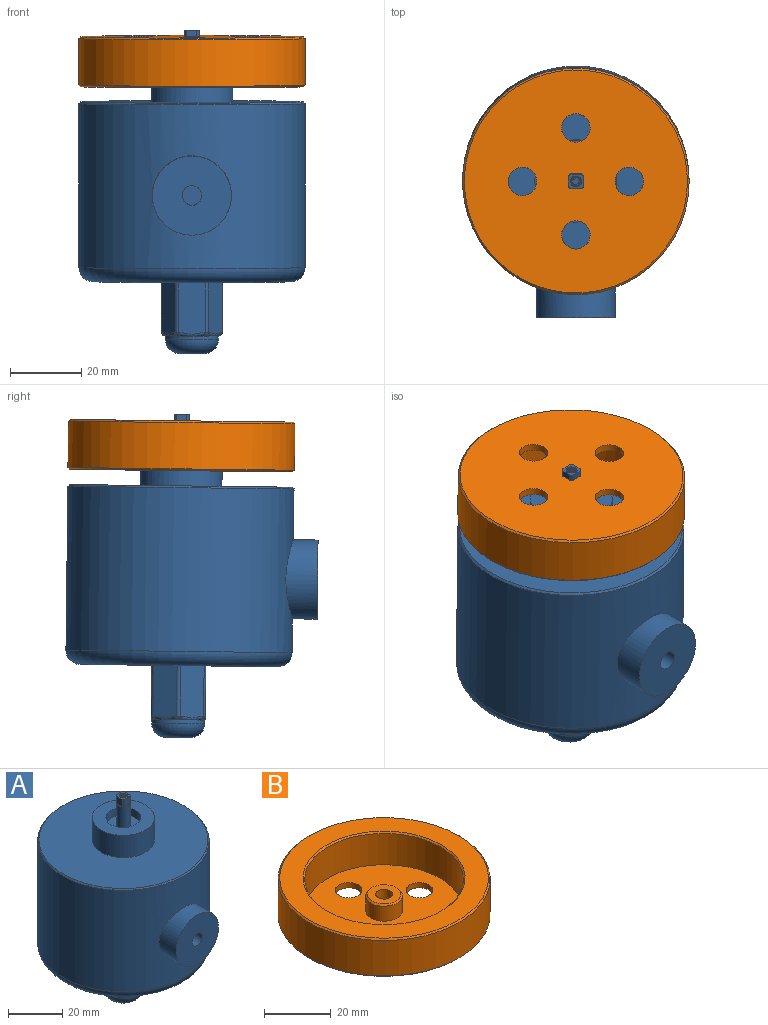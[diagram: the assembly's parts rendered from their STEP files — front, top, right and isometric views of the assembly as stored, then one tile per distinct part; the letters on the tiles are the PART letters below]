
ASSEMBLY  parts=2 mates=1
PART A: 73 faces, bbox 68.9x73.2x91.1 mm
  f0: plane 2.88x2.87mm, normal (0,0,1), area 5.9mm2, adj f69,f70,f71,f72
  f1: plane 4.31x4.31mm, normal (0,0,1), area 10.6mm2, adj f2,f60,f62,f64,f66,f69,f70,f71
  f2: cylinder r=2.5mm len=13.5mm, axis (0,0,-1), area 173.5mm2, adj f1,f58,f59,f60,f61,f62,f63,f64
  f3: plane 0.53x0.31mm, normal (0,0,-1), area 0.1mm2, adj f24,f29,f30
  f4: plane 0.53x0.31mm, normal (0,0,-1), area 0.1mm2, adj f24,f35,f40
  f5: plane 0.61x0.18mm, normal (0,0,-1), area 0.1mm2, adj f24,f45,f50
  f6: plane 0.53x0.31mm, normal (0,0,-1), area 0.1mm2, adj f24,f53,f54
  f7: plane 0.61x0.18mm, normal (0,0,-1), area 0.1mm2, adj f24,f34,f39
  f8: plane 55.5x55.5mm, normal (0,0,-1), area 2219.5mm2, adj f13,f17,f18,f19,f20,f21,f22,f27
  f9: cylinder r=31.75mm len=63.5mm, axis (0,0,-1), area 8773.2mm2, adj f11,f13,f14
  f10: plane 62.5x62.5mm, normal (0,0,1), area 2652.5mm2, adj f14,f15
  f11: cylinder r=11.11mm len=22.21mm, axis (0,1,0), area 551mm2, adj f9,f12
  f12: plane 22.21x22.21mm, normal (0,-1,0), area 363.7mm2, adj f11,f67
  f13: torus R=27.75mm, axis (0,0,1), area 1196.1mm2, adj f8,f9
  f14: cone r=31.25mm half-angle=45deg, axis (0,0,-1), area 140mm2, adj f9,f10
  f15: cylinder r=11.5mm len=23mm, axis (0,0,-1), area 727.6mm2, adj f10,f16
  f16: plane 23x23mm, normal (0,0,1), area 284.8mm2, adj f15,f57
  f17: plane 14.67x7.62mm, normal (0,-1,0), area 109.8mm2, adj f8,f43,f49,f51,f53,f56
  f18: plane 14.67x6.6mm, normal (-0.87,-0.5,0), area 109.8mm2, adj f8,f46,f50,f52,f54,f56
  f19: plane 14.67x6.6mm, normal (-0.87,0.5,0), area 109.8mm2, adj f8,f36,f40,f42,f45,f46
  f20: plane 14.67x7.62mm, normal (0,1,0), area 109.8mm2, adj f8,f27,f30,f32,f35,f36
  f21: plane 14.67x6.6mm, normal (0.87,0.5,0), area 109.8mm2, adj f8,f27,f29,f31,f33,f34
  f22: plane 14.67x6.6mm, normal (0.87,-0.5,0), area 109.8mm2, adj f8,f33,f39,f41,f43,f44
  f23: plane 0.53x0.31mm, normal (0,0,-1), area 0.1mm2, adj f24,f44,f49
  f24: cylinder r=7.45mm len=14.9mm, axis (0,0,1), area 46.8mm2, adj f3,f4,f5,f6,f7,f23,f26,f31
  f25: plane 6.9x6.9mm, normal (0,0,-1), area 37.4mm2, adj f26
  f26: torus R=3.45mm, axis (0,0,-1), area 236.7mm2, adj f24,f25
  f27: cylinder r=1mm len=14.2mm, axis (0,0,1), area 14.9mm2, adj f8,f20,f21,f28
  f28: sphere r=1mm, area 1mm2, adj f27,f29,f30
  f29: cylinder r=1mm len=1.04mm, axis (-0.5,0.87,0), area 0.6mm2, adj f3,f21,f28,f31
  f30: cylinder r=1mm len=1mm, axis (-1,0,0), area 0.6mm2, adj f3,f20,f28,f32
  f31: bspline ~6.49x4.32mm, area 6.5mm2, adj f21,f24,f29,f34
  f32: bspline ~6.91x1mm, area 6.5mm2, adj f20,f24,f30,f35
  f33: cylinder r=1mm len=14.2mm, axis (0,0,1), area 14.9mm2, adj f8,f21,f22,f37
  f34: cylinder r=1mm len=1.04mm, axis (-0.5,0.87,0), area 0.6mm2, adj f7,f21,f31,f37
  f35: cylinder r=1mm len=1mm, axis (-1,0,0), area 0.6mm2, adj f4,f20,f32,f38
  f36: cylinder r=1mm len=14.2mm, axis (0,0,1), area 14.9mm2, adj f8,f19,f20,f38
  f37: sphere r=1mm, area 1mm2, adj f33,f34,f39
  f38: sphere r=1mm, area 1mm2, adj f35,f36,f40
  f39: cylinder r=1mm len=1.04mm, axis (0.5,0.87,0), area 0.6mm2, adj f7,f22,f37,f41
  f40: cylinder r=1mm len=1.04mm, axis (-0.5,-0.87,0), area 0.6mm2, adj f4,f19,f38,f42
  f41: bspline ~6.49x4.32mm, area 6.5mm2, adj f22,f24,f39,f44
  f42: bspline ~6.49x4.32mm, area 6.5mm2, adj f19,f24,f40,f45
  f43: cylinder r=1mm len=14.2mm, axis (0,0,1), area 14.9mm2, adj f8,f17,f22,f47
  f44: cylinder r=1mm len=1.04mm, axis (0.5,0.87,0), area 0.6mm2, adj f22,f23,f41,f47
  f45: cylinder r=1mm len=1.04mm, axis (-0.5,-0.87,0), area 0.6mm2, adj f5,f19,f42,f48
  f46: cylinder r=1mm len=14.2mm, axis (0,0,1), area 14.9mm2, adj f8,f18,f19,f48
  f47: sphere r=1mm, area 1mm2, adj f43,f44,f49
  f48: sphere r=1mm, area 1mm2, adj f45,f46,f50
  f49: cylinder r=1mm len=1mm, axis (1,0,0), area 0.6mm2, adj f17,f23,f47,f51
  f50: cylinder r=1mm len=1.04mm, axis (0.5,-0.87,0), area 0.6mm2, adj f5,f18,f48,f52
  f51: bspline ~6.91x1mm, area 6.5mm2, adj f17,f24,f49,f53
  f52: bspline ~6.49x4.32mm, area 6.5mm2, adj f18,f24,f50,f54
  f53: cylinder r=1mm len=1mm, axis (1,0,0), area 0.6mm2, adj f6,f17,f51,f55
  f54: cylinder r=1mm len=1.04mm, axis (0.5,-0.87,0), area 0.6mm2, adj f6,f18,f52,f55
  f55: sphere r=1mm, area 1mm2, adj f53,f54,f56
  f56: cylinder r=1mm len=14.2mm, axis (0,0,1), area 14.9mm2, adj f8,f17,f18,f55
  f57: cylinder r=6.45mm len=12.9mm, axis (0,0,1), area 141.8mm2, adj f16,f58
  f58: plane 12.9x12.9mm, normal (0,0,1), area 111.1mm2, adj f2,f57
  f59: plane 2.76x0.42mm, normal (0,0,1), area 0.8mm2, adj f2,f60
  f60: plane 3.3x2.76mm, normal (1,0,0), area 9.1mm2, adj f1,f2,f59
  f61: plane 2.76x0.42mm, normal (0,0,1), area 0.8mm2, adj f2,f62
  f62: plane 3.3x2.76mm, normal (0,-1,0), area 9.1mm2, adj f1,f2,f61
  f63: plane 2.76x0.42mm, normal (0,0,1), area 0.8mm2, adj f2,f64
  f64: plane 3.3x2.76mm, normal (-1,0,0), area 9.1mm2, adj f1,f2,f63
  f65: plane 2.76x0.42mm, normal (0,0,1), area 0.8mm2, adj f2,f66
  f66: plane 3.3x2.76mm, normal (0,1,0), area 9.1mm2, adj f1,f2,f65
  f67: cylinder r=2.75mm len=6.9mm, axis (0,-1,0), area 119.2mm2, adj f12,f68
  f68: plane 5.5x5.5mm, normal (0,-1,0), area 23.8mm2, adj f67
  f69: bspline ~10.32x3.51mm, area 54.1mm2, adj f0,f1,f71,f72
  f70: bspline ~10.41x3.51mm, area 54.7mm2, adj f0,f1,f71,f72
  f71: bspline ~10.23x3.56mm, area 13.9mm2, adj f0,f1,f69,f70
  f72: cylinder r=1.25mm len=10mm, axis (0,0,-1), area 45.6mm2, adj f0,f1,f69,f70
PART B: 32 faces, bbox 63.6x63.6x14 mm
  f0: cylinder r=0.75mm len=1.5mm, axis (0,0,1), area 1.8mm2, adj f9,f12,f13,f27,f28,f29
  f1: cylinder r=0.75mm len=1.5mm, axis (0,0,-1), area 1.8mm2, adj f9,f10,f12,f26,f29,f31
  f2: cylinder r=0.75mm len=1.5mm, axis (0,0,-1), area 1.8mm2, adj f9,f11,f13,f25,f28,f30
  f3: cylinder r=0.75mm len=1.5mm, axis (0,0,1), area 1.8mm2, adj f9,f10,f11,f24,f30,f31
  f4: cylinder r=4mm len=8mm, axis (0,0,-1), area 50.3mm2, adj f8,f9
  f5: cylinder r=4mm len=8mm, axis (0,0,-1), area 50.3mm2, adj f8,f9
  f6: cylinder r=4mm len=8mm, axis (0,0,-1), area 50.3mm2, adj f8,f9
  f7: cylinder r=31.8mm len=63.6mm, axis (0,0,-1), area 2597.5mm2, adj f21,f22
  f8: plane 47.6x47.6mm, normal (0,0,1), area 1483.4mm2, adj f4,f5,f6,f15,f17,f19
  f9: plane 62.6x62.6mm, normal (0,0,-1), area 2859.6mm2, adj f0,f1,f2,f3,f4,f5,f6,f10
  f10: plane 2.7x1.5mm, normal (-1,0,0), area 4mm2, adj f1,f3,f9,f31
  f11: plane 2.7x1.5mm, normal (0,1,0), area 4mm2, adj f2,f3,f9,f30
  f12: plane 2.7x1.5mm, normal (0,-1,0), area 4mm2, adj f0,f1,f9,f29
  f13: plane 2.7x1.5mm, normal (1,0,0), area 4mm2, adj f0,f2,f9,f28
  f14: cylinder r=2.5mm len=6.5mm, axis (0,0,-1), area 102.1mm2, adj f16,f24,f25,f26,f27,f28,f29,f30
  f15: cylinder r=5.5mm len=11mm, axis (0,0,-1), area 190.1mm2, adj f8,f23
  f16: plane 10x10mm, normal (0,0,1), area 58.9mm2, adj f14,f23
  f17: cylinder r=23.8mm len=47.6mm, axis (0,0,-1), area 1719.7mm2, adj f8,f20
  f18: plane 62.6x62.6mm, normal (0,0,1), area 1222.7mm2, adj f20,f21
  f19: cylinder r=4mm len=8mm, axis (0,0,-1), area 50.3mm2, adj f8,f9
  f20: cone r=23.8mm half-angle=45deg, axis (0,0,1), area 106.9mm2, adj f17,f18
  f21: cone r=31.3mm half-angle=45deg, axis (0,0,-1), area 140.2mm2, adj f7,f18
  f22: cone r=31.8mm half-angle=45deg, axis (0,0,1), area 140.2mm2, adj f7,f9
  f23: cone r=5mm half-angle=45deg, axis (0,0,-1), area 23.3mm2, adj f15,f16
  f24: plane 0.74x0.74mm, normal (0,0,-1), area 0.1mm2, adj f3,f14
  f25: plane 0.74x0.74mm, normal (0,0,-1), area 0.1mm2, adj f2,f14
  f26: plane 0.74x0.74mm, normal (0,0,-1), area 0.1mm2, adj f1,f14
  f27: plane 0.74x0.74mm, normal (0,0,-1), area 0.1mm2, adj f0,f14
  f28: plane 2.71x0.4mm, normal (0,0,1), area 0.7mm2, adj f0,f2,f13,f14
  f29: plane 2.71x0.4mm, normal (0,0,1), area 0.7mm2, adj f0,f1,f12,f14
  f30: plane 2.71x0.4mm, normal (0,0,1), area 0.7mm2, adj f2,f3,f11,f14
  f31: plane 2.71x0.4mm, normal (0,0,1), area 0.7mm2, adj f1,f3,f10,f14
PLACE A rot(axis=(1,0,0),0.7deg) t=(0,22.97,30.02)mm
PLACE B rot(axis=(-1,0,0),179.3deg) t=(0,22.16,98.74)mm
MATE revolute A.f2 <-> B.f14  axis (0,-0.01,1) through (0,22.17,97.24)mm
